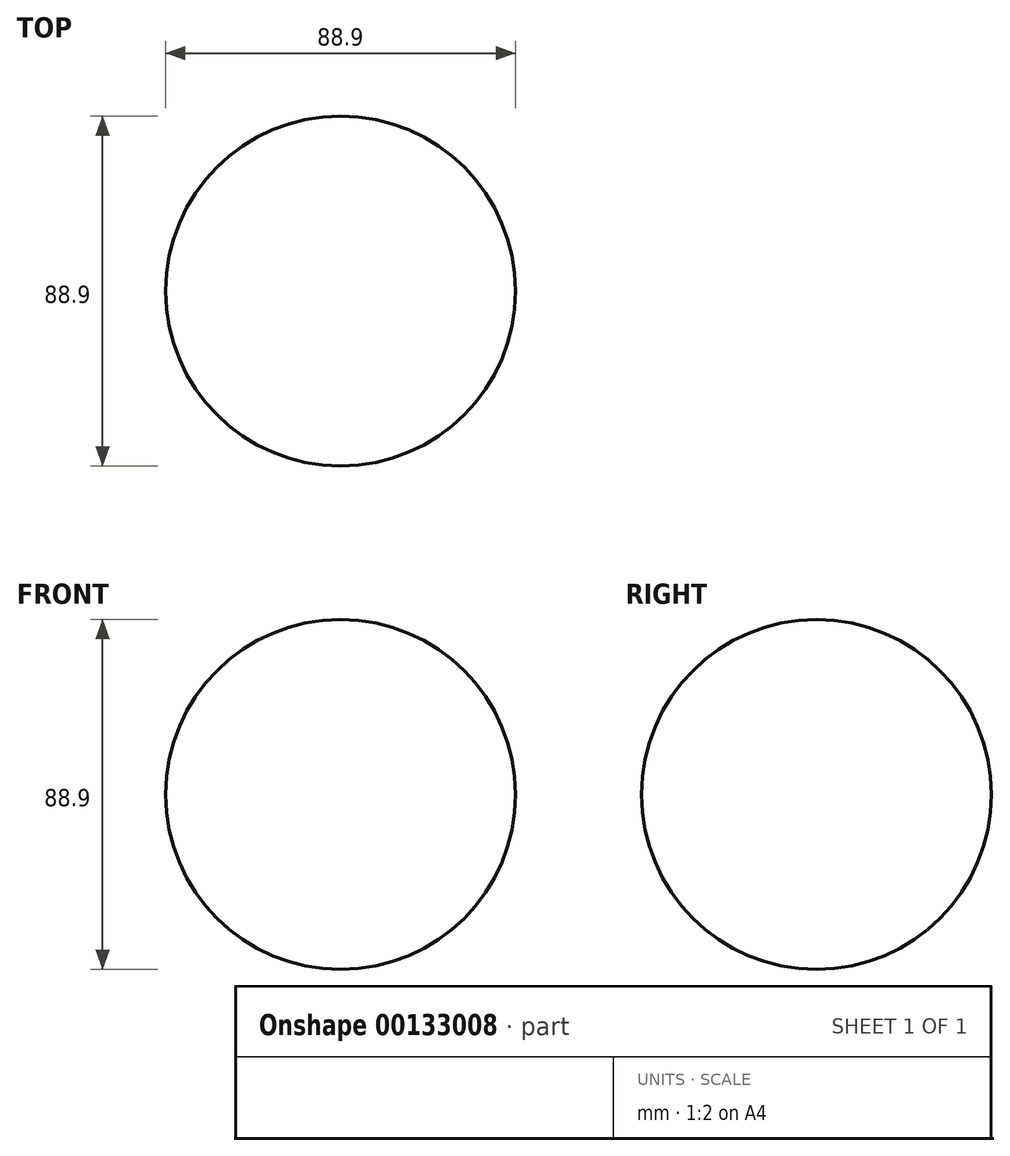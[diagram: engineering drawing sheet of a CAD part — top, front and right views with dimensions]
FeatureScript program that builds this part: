
annotation { "Feature Type Name" : "Feature", "Feature Type Description" : "" }
export const myFeature = defineFeature(function(context is Context, id is Id, definition is map)
    precondition{}
    {
        {
            var Q0;
            Q0=qCreatedBy(makeId("Front.planeOp"),FACE);
            var sketch = newSketch(context, id + "F0", { "sketchPlane" : qUnion([Q0])});
            skArc(sketch, "E0", {"start": v(0, 0) * mm, "mid": v(44.45, 44.45) * mm, "end": v(0, 88.9) * mm});
            skLineSegment(sketch, "E1", {"start": v(0, 88.9) * mm, "end": v(0, 0) * mm});
            skSolve(sketch);
        }
        {
            var Q0;
            Q0 = qSketchRegion(id + "F0", true);
            var Q1;
            Q1=sQuery(id+"F0.wireOp",EDGE,"E1");
            revolve(context, id + "F1", {"entities" : qUnion([Q0]), "axis" : qUnion([Q1]), "revolveType" : RevolveType.FULL});
        }
    });
